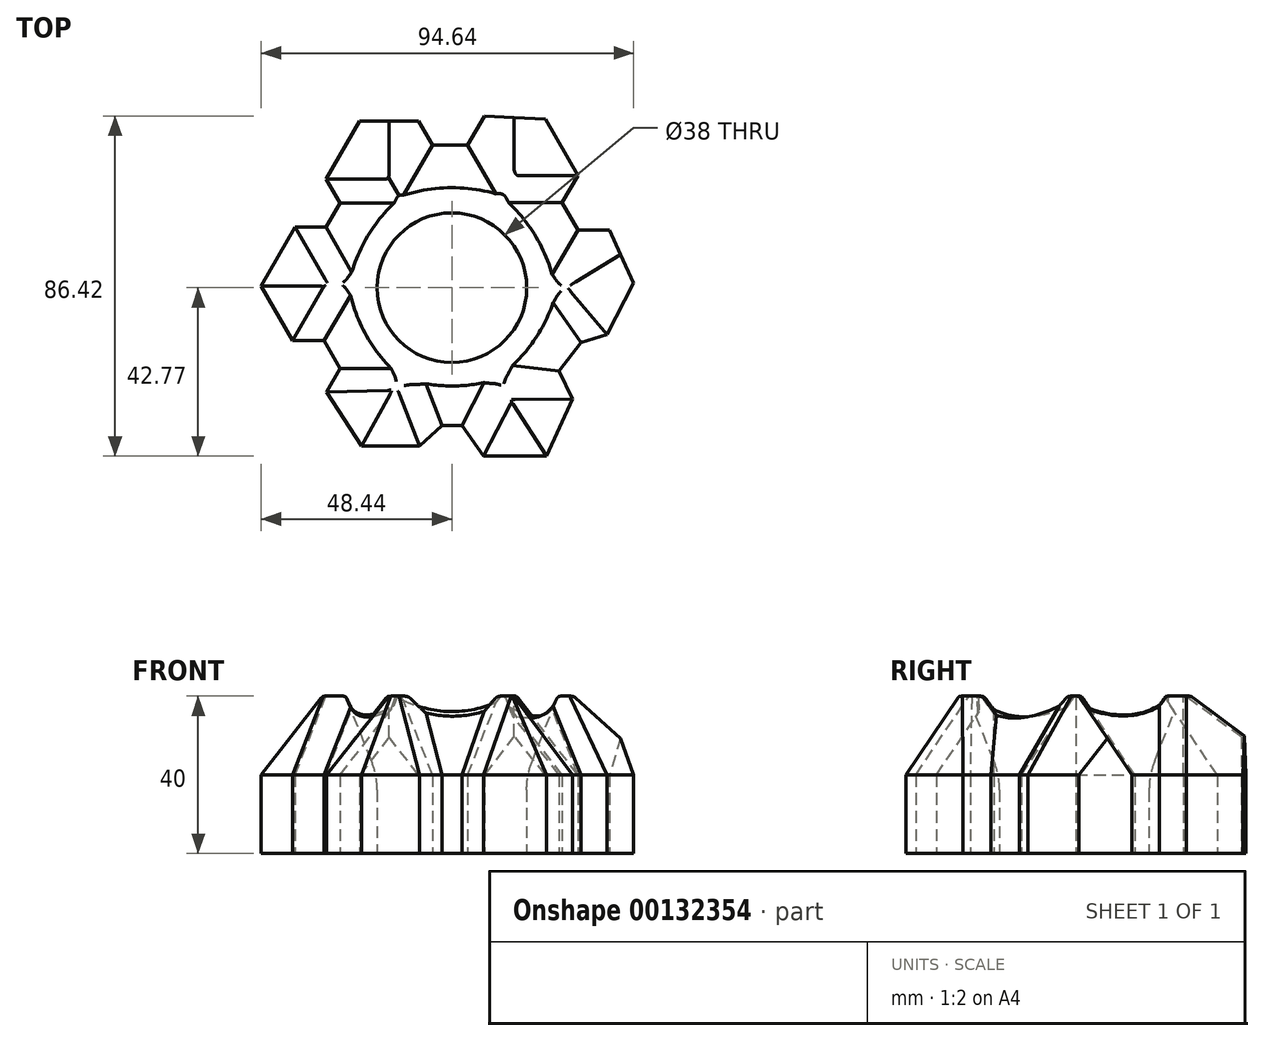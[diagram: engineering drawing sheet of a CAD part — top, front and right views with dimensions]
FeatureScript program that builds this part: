
annotation { "Feature Type Name" : "Feature", "Feature Type Description" : "" }
export const myFeature = defineFeature(function(context is Context, id is Id, definition is map)
    precondition{}
    {
        {
            var Q0;
            Q0=qCreatedBy(makeId("Top.planeOp"),FACE);
            var sketch = newSketch(context, id + "F0", { "sketchPlane" : qUnion([Q0])});
            skLineSegment(sketch, "E0", {"start": v(-48.44, 0.38) * mm, "end": v(-39.8, 15.35) * mm});
            skLineSegment(sketch, "E1", {"start": v(-39.8, 15.35) * mm, "end": v(-31.98, 15.35) * mm});
            skLineSegment(sketch, "E2", {"start": v(-31.98, 15.35) * mm, "end": v(-28.4, 21.56) * mm});
            skLineSegment(sketch, "E3", {"start": v(-28.4, 21.56) * mm, "end": v(-31.92, 27.66) * mm});
            skLineSegment(sketch, "E4", {"start": v(-31.92, 27.66) * mm, "end": v(-23.42, 42.38) * mm});
            skLineSegment(sketch, "E5", {"start": v(-23.42, 42.38) * mm, "end": v(-8.47, 42.38) * mm});
            skLineSegment(sketch, "E6", {"start": v(-8.47, 42.38) * mm, "end": v(-4.96, 36.29) * mm});
            skLineSegment(sketch, "E7", {"start": v(-4.96, 36.29) * mm, "end": v(4.04, 36.29) * mm});
            skLineSegment(sketch, "E8", {"start": v(4.04, 36.29) * mm, "end": v(8.3, 43.65) * mm});
            skLineSegment(sketch, "E9", {"start": v(8.3, 43.65) * mm, "end": v(23.77, 42.82) * mm});
            skLineSegment(sketch, "E10", {"start": v(23.77, 42.82) * mm, "end": v(32.02, 28.53) * mm});
            skLineSegment(sketch, "E11", {"start": v(32.02, 28.53) * mm, "end": v(28.02, 21.6) * mm});
            skLineSegment(sketch, "E12", {"start": v(28.02, 21.6) * mm, "end": v(32.02, 14.67) * mm});
            skLineSegment(sketch, "E13", {"start": v(32.02, 14.67) * mm, "end": v(40.02, 14.67) * mm});
            skLineSegment(sketch, "E14", {"start": v(-48.44, 0.38) * mm, "end": v(-40.44, -13.47) * mm});
            skLineSegment(sketch, "E15", {"start": v(-40.44, -13.47) * mm, "end": v(-32.44, -13.47) * mm});
            skLineSegment(sketch, "E16", {"start": v(-32.44, -13.47) * mm, "end": v(-28.4, -20.47) * mm});
            skLineSegment(sketch, "E17", {"start": v(-28.4, -20.47) * mm, "end": v(-31.85, -26.44) * mm});
            skLineSegment(sketch, "E18", {"start": v(24.09, -42.77) * mm, "end": v(8.09, -42.77) * mm});
            skLineSegment(sketch, "E19", {"start": v(8.09, -42.77) * mm, "end": v(2.53, -35.02) * mm});
            skCircle(sketch, "E20", {"center": v(0, 0) * mm, "radius": 19 * mm});
            skLineSegment(sketch, "E21", {"start": v(2.53, -35.02) * mm, "end": v(-2.47, -35.02) * mm});
            skLineSegment(sketch, "E22", {"start": v(-2.47, -35.02) * mm, "end": v(-8.17, -40.27) * mm});
            skLineSegment(sketch, "E23", {"start": v(-8.17, -40.27) * mm, "end": v(-22.93, -40.27) * mm});
            skLineSegment(sketch, "E24", {"start": v(-22.93, -40.27) * mm, "end": v(-31.85, -26.44) * mm});
            skLineSegment(sketch, "E25", {"start": v(40.02, 14.67) * mm, "end": v(46.2, 1.16) * mm});
            skLineSegment(sketch, "E26", {"start": v(46.2, 1.16) * mm, "end": v(39.38, -11.85) * mm});
            skLineSegment(sketch, "E27", {"start": v(39.38, -11.85) * mm, "end": v(32.82, -13.96) * mm});
            skLineSegment(sketch, "E28", {"start": v(32.82, -13.96) * mm, "end": v(27.24, -21.14) * mm});
            skLineSegment(sketch, "E29", {"start": v(27.24, -21.14) * mm, "end": v(30.59, -28.33) * mm});
            skLineSegment(sketch, "E30", {"start": v(30.59, -28.33) * mm, "end": v(24.09, -42.77) * mm});
            skSolve(sketch);
        }
        {
            var Q0;
            Q0 = qSketchRegion(id + "F0", true);
            extrude(context, id + "F1", {"entities" : qUnion([Q0]), "depth" : 40 * mm});
        }
        {
            var Q0;
            Q0=makeQuery(id+"F1.opExtrude","CAP_EDGE",EDGE,{"disambiguationData":[OSD([sQuery(id+"F0.wireOp",EDGE,"QNCMXTpP-GXVm-6eRc-1OdR-BgQgE8rH5RGP")])],"isStart":false});
            var Q1;
            Q1=makeQuery(id+"F1.opExtrude","CAP_EDGE",EDGE,{"disambiguationData":[OSD([sQuery(id+"F0.wireOp",EDGE,"32e85595-2d38-4c8c-88ba-0e2045ae9be3.filletArc")])],"isStart":false});
            var Q2;
            Q2=makeQuery(id+"F1.opExtrude","CAP_EDGE",EDGE,{"disambiguationData":[OSD([sQuery(id+"F0.wireOp",EDGE,"7Lfb2Pw1-ovII-kQZP-8tTO-OoWHJU2uK7MA")])],"isStart":false});
            var Q3;
            Q3=makeQuery(id+"F1.opExtrude","CAP_EDGE",EDGE,{"disambiguationData":[OSD([sQuery(id+"F0.wireOp",EDGE,"GPxmBkKN-ensr-DpaE-CKd3-DWqYEm3aYaC1")])],"isStart":false});
            var Q4;
            Q4=makeQuery(id+"F1.opExtrude","CAP_EDGE",EDGE,{"disambiguationData":[OSD([sQuery(id+"F0.wireOp",EDGE,"cDQV9YWy-g1bv-AJuI-bAqr-Qak8u58BYPGV")])],"isStart":false});
            var Q5;
            Q5=makeQuery(id+"F1.opExtrude","CAP_EDGE",EDGE,{"disambiguationData":[OSD([sQuery(id+"F0.wireOp",EDGE,"83e46631-e496-48b3-ba96-4f3d211e591d.filletArc")])],"isStart":false});
            var Q6;
            Q6=makeQuery(id+"F1.opExtrude","CAP_EDGE",EDGE,{"disambiguationData":[OSD([sQuery(id+"F0.wireOp",EDGE,"998c5da3-717e-4341-962a-c66db3e48c3c.filletArc")])],"isStart":false});
            var Q7;
            Q7=makeQuery(id+"F1.opExtrude","CAP_EDGE",EDGE,{"disambiguationData":[OSD([sQuery(id+"F0.wireOp",EDGE,"pI0UNvur-lg5A-7E1c-7WQA-sV9YhzP1md2U")])],"isStart":false});
            var Q8;
            Q8=makeQuery(id+"F1.opExtrude","CAP_EDGE",EDGE,{"disambiguationData":[OSD([sQuery(id+"F0.wireOp",EDGE,"E13")])],"isStart":false});
            var Q9;
            Q9=makeQuery(id+"F1.opExtrude","CAP_EDGE",EDGE,{"disambiguationData":[OSD([sQuery(id+"F0.wireOp",EDGE,"E12")])],"isStart":false});
            var Q10;
            Q10=makeQuery(id+"F1.opExtrude","CAP_EDGE",EDGE,{"disambiguationData":[OSD([sQuery(id+"F0.wireOp",EDGE,"E11")])],"isStart":false});
            var Q11;
            Q11=makeQuery(id+"F1.opExtrude","CAP_EDGE",EDGE,{"disambiguationData":[OSD([sQuery(id+"F0.wireOp",EDGE,"E10")])],"isStart":false});
            var Q12;
            Q12=makeQuery(id+"F1.opExtrude","CAP_EDGE",EDGE,{"disambiguationData":[OSD([sQuery(id+"F0.wireOp",EDGE,"E9")])],"isStart":false});
            var Q13;
            Q13=makeQuery(id+"F1.opExtrude","CAP_EDGE",EDGE,{"disambiguationData":[OSD([sQuery(id+"F0.wireOp",EDGE,"E8")])],"isStart":false});
            var Q14;
            Q14=makeQuery(id+"F1.opExtrude","CAP_EDGE",EDGE,{"disambiguationData":[OSD([sQuery(id+"F0.wireOp",EDGE,"E7")])],"isStart":false});
            var Q15;
            Q15=makeQuery(id+"F1.opExtrude","CAP_EDGE",EDGE,{"disambiguationData":[OSD([sQuery(id+"F0.wireOp",EDGE,"E6")])],"isStart":false});
            var Q16;
            Q16=makeQuery(id+"F1.opExtrude","CAP_EDGE",EDGE,{"disambiguationData":[OSD([sQuery(id+"F0.wireOp",EDGE,"E5")])],"isStart":false});
            var Q17;
            Q17=makeQuery(id+"F1.opExtrude","CAP_EDGE",EDGE,{"disambiguationData":[OSD([sQuery(id+"F0.wireOp",EDGE,"E4")])],"isStart":false});
            var Q18;
            Q18=makeQuery(id+"F1.opExtrude","CAP_EDGE",EDGE,{"disambiguationData":[OSD([sQuery(id+"F0.wireOp",EDGE,"E3")])],"isStart":false});
            var Q19;
            Q19=makeQuery(id+"F1.opExtrude","CAP_EDGE",EDGE,{"disambiguationData":[OSD([sQuery(id+"F0.wireOp",EDGE,"E2")])],"isStart":false});
            var Q20;
            Q20=makeQuery(id+"F1.opExtrude","CAP_EDGE",EDGE,{"disambiguationData":[OSD([sQuery(id+"F0.wireOp",EDGE,"E1")])],"isStart":false});
            var Q21;
            Q21=makeQuery(id+"F1.opExtrude","CAP_EDGE",EDGE,{"disambiguationData":[OSD([sQuery(id+"F0.wireOp",EDGE,"E0")])],"isStart":false});
            var Q22;
            Q22=makeQuery(id+"F1.opExtrude","CAP_EDGE",EDGE,{"disambiguationData":[OSD([sQuery(id+"F0.wireOp",EDGE,"E14")])],"isStart":false});
            var Q23;
            Q23=makeQuery(id+"F1.opExtrude","CAP_EDGE",EDGE,{"disambiguationData":[OSD([sQuery(id+"F0.wireOp",EDGE,"E15")])],"isStart":false});
            var Q24;
            Q24=makeQuery(id+"F1.opExtrude","CAP_EDGE",EDGE,{"disambiguationData":[OSD([sQuery(id+"F0.wireOp",EDGE,"E16")])],"isStart":false});
            var Q25;
            Q25=makeQuery(id+"F1.opExtrude","CAP_EDGE",EDGE,{"disambiguationData":[OSD([sQuery(id+"F0.wireOp",EDGE,"E17")])],"isStart":false});
            var Q26;
            Q26=makeQuery(id+"F1.opExtrude","CAP_EDGE",EDGE,{"disambiguationData":[OSD([sQuery(id+"F0.wireOp",EDGE,"E24")])],"isStart":false});
            var Q27;
            Q27=makeQuery(id+"F1.opExtrude","CAP_EDGE",EDGE,{"disambiguationData":[OSD([sQuery(id+"F0.wireOp",EDGE,"E23")])],"isStart":false});
            var Q28;
            Q28=makeQuery(id+"F1.opExtrude","CAP_EDGE",EDGE,{"disambiguationData":[OSD([sQuery(id+"F0.wireOp",EDGE,"E22")])],"isStart":false});
            var Q29;
            Q29=makeQuery(id+"F1.opExtrude","CAP_EDGE",EDGE,{"disambiguationData":[OSD([sQuery(id+"F0.wireOp",EDGE,"E21")])],"isStart":false});
            var Q30;
            Q30=makeQuery(id+"F1.opExtrude","CAP_EDGE",EDGE,{"disambiguationData":[OSD([sQuery(id+"F0.wireOp",EDGE,"E19")])],"isStart":false});
            var Q31;
            Q31=makeQuery(id+"F1.opExtrude","CAP_EDGE",EDGE,{"disambiguationData":[OSD([sQuery(id+"F0.wireOp",EDGE,"E18")])],"isStart":false});
            var Q32;
            Q32=makeQuery(id+"F1.opExtrude","CAP_EDGE",EDGE,{"disambiguationData":[OSD([sQuery(id+"F0.wireOp",EDGE,"E30")])],"isStart":false});
            var Q33;
            Q33=makeQuery(id+"F1.opExtrude","CAP_EDGE",EDGE,{"disambiguationData":[OSD([sQuery(id+"F0.wireOp",EDGE,"E29")])],"isStart":false});
            var Q34;
            Q34=makeQuery(id+"F1.opExtrude","CAP_EDGE",EDGE,{"disambiguationData":[OSD([sQuery(id+"F0.wireOp",EDGE,"E28")])],"isStart":false});
            var Q35;
            Q35=makeQuery(id+"F1.opExtrude","CAP_EDGE",EDGE,{"disambiguationData":[OSD([sQuery(id+"F0.wireOp",EDGE,"E27")])],"isStart":false});
            var Q36;
            Q36=makeQuery(id+"F1.opExtrude","CAP_EDGE",EDGE,{"disambiguationData":[OSD([sQuery(id+"F0.wireOp",EDGE,"E26")])],"isStart":false});
            var Q37;
            Q37=makeQuery(id+"F1.opExtrude","CAP_EDGE",EDGE,{"disambiguationData":[OSD([sQuery(id+"F0.wireOp",EDGE,"E25")])],"isStart":false});
            chamfer(context, id + "F2", {"entities" : qUnion([Q0, Q1, Q2, Q3, Q4, Q5, Q6, Q7, Q8, Q9, Q10, Q11, Q12, Q13, Q14, Q15, Q16, Q17, Q18, Q19, Q20, Q21, Q22, Q23, Q24, Q25, Q26, Q27, Q28, Q29, Q30, Q31, Q32, Q33, Q34, Q35, Q36, Q37]), "chamferType" : ChamferType.TWO_OFFSETS, "width1" : 20 * mm, "oppositeDirection" : false, "width2" : 13.5 * mm, "tangentPropagation" : true});
        }
        {
            var Q0;
            Q0=makeQuery(id+"F1.opExtrude","CAP_EDGE",EDGE,{"disambiguationData":[OSD([sQuery(id+"F0.wireOp",EDGE,"E20")])],"isStart":false});
            chamfer(context, id + "F3", {"entities" : qUnion([Q0]), "chamferType" : ChamferType.TWO_OFFSETS, "width1" : 20 * mm, "oppositeDirection" : false, "width2" : 8 * mm, "tangentPropagation" : true});
        }
        {
            var Q0;
            Q0=makeQuery(id+"F3.opChamfer","SPLIT",FACE,{"disambiguationData":[OD(0.0)],"derivedFrom":makeQuery(id+"F1.opExtrude","CAP_FACE",FACE,{"disambiguationData":[OSD([sQuery(id+"F0.wireOp",EDGE,"E0"),sQuery(id+"F0.wireOp",EDGE,"E1"),sQuery(id+"F0.wireOp",EDGE,"E2"),sQuery(id+"F0.wireOp",EDGE,"E3"),sQuery(id+"F0.wireOp",EDGE,"E4"),sQuery(id+"F0.wireOp",EDGE,"E5"),sQuery(id+"F0.wireOp",EDGE,"E6"),sQuery(id+"F0.wireOp",EDGE,"E7"),sQuery(id+"F0.wireOp",EDGE,"E8"),sQuery(id+"F0.wireOp",EDGE,"E9"),sQuery(id+"F0.wireOp",EDGE,"E10"),sQuery(id+"F0.wireOp",EDGE,"E11"),sQuery(id+"F0.wireOp",EDGE,"E12"),sQuery(id+"F0.wireOp",EDGE,"E13"),sQuery(id+"F0.wireOp",EDGE,"E14"),sQuery(id+"F0.wireOp",EDGE,"E15"),sQuery(id+"F0.wireOp",EDGE,"E16"),sQuery(id+"F0.wireOp",EDGE,"E17"),sQuery(id+"F0.wireOp",EDGE,"E18"),sQuery(id+"F0.wireOp",EDGE,"E19"),sQuery(id+"F0.wireOp",EDGE,"E20"),sQuery(id+"F0.wireOp",EDGE,"E21"),sQuery(id+"F0.wireOp",EDGE,"E22"),sQuery(id+"F0.wireOp",EDGE,"E23"),sQuery(id+"F0.wireOp",EDGE,"E24"),sQuery(id+"F0.wireOp",EDGE,"E25"),sQuery(id+"F0.wireOp",EDGE,"E26"),sQuery(id+"F0.wireOp",EDGE,"E27"),sQuery(id+"F0.wireOp",EDGE,"E28"),sQuery(id+"F0.wireOp",EDGE,"E29"),sQuery(id+"F0.wireOp",EDGE,"E30")])],"isStart":false})});
            var Q1;
            {var subQ0=sQuery(id+"F0.wireOp",EDGE,"E6");Q1=makeQuery(id+"F2.opChamfer","BLEND_EDGE",EDGE,{"blendedFrom":[makeQuery(id+"F1.opExtrude","CAP_EDGE",EDGE,{"disambiguationData":[OSD([subQ0])],"isStart":false}),makeQuery(id+"F1.opExtrude","CAP_FACE",FACE,{"disambiguationData":[OSD([sQuery(id+"F0.wireOp",EDGE,"E0"),sQuery(id+"F0.wireOp",EDGE,"E1"),sQuery(id+"F0.wireOp",EDGE,"E2"),sQuery(id+"F0.wireOp",EDGE,"E3"),sQuery(id+"F0.wireOp",EDGE,"E4"),sQuery(id+"F0.wireOp",EDGE,"E5"),subQ0,sQuery(id+"F0.wireOp",EDGE,"E7"),sQuery(id+"F0.wireOp",EDGE,"E8"),sQuery(id+"F0.wireOp",EDGE,"E9"),sQuery(id+"F0.wireOp",EDGE,"E10"),sQuery(id+"F0.wireOp",EDGE,"E11"),sQuery(id+"F0.wireOp",EDGE,"E12"),sQuery(id+"F0.wireOp",EDGE,"E13"),sQuery(id+"F0.wireOp",EDGE,"E14"),sQuery(id+"F0.wireOp",EDGE,"E15"),sQuery(id+"F0.wireOp",EDGE,"E16"),sQuery(id+"F0.wireOp",EDGE,"E17"),sQuery(id+"F0.wireOp",EDGE,"E18"),sQuery(id+"F0.wireOp",EDGE,"E19"),sQuery(id+"F0.wireOp",EDGE,"E20"),sQuery(id+"F0.wireOp",EDGE,"E21"),sQuery(id+"F0.wireOp",EDGE,"E22"),sQuery(id+"F0.wireOp",EDGE,"E23"),sQuery(id+"F0.wireOp",EDGE,"E24"),sQuery(id+"F0.wireOp",EDGE,"E25"),sQuery(id+"F0.wireOp",EDGE,"E26"),sQuery(id+"F0.wireOp",EDGE,"E27"),sQuery(id+"F0.wireOp",EDGE,"E28"),sQuery(id+"F0.wireOp",EDGE,"E29"),sQuery(id+"F0.wireOp",EDGE,"E30")])],"isStart":false})],"blendedInto":[makeQuery(id+"F1.opExtrude","CAP_FACE",FACE,{"disambiguationData":[OSD([sQuery(id+"F0.wireOp",EDGE,"E0"),sQuery(id+"F0.wireOp",EDGE,"E1"),sQuery(id+"F0.wireOp",EDGE,"E2"),sQuery(id+"F0.wireOp",EDGE,"E3"),sQuery(id+"F0.wireOp",EDGE,"E4"),sQuery(id+"F0.wireOp",EDGE,"E5"),subQ0,sQuery(id+"F0.wireOp",EDGE,"E7"),sQuery(id+"F0.wireOp",EDGE,"E8"),sQuery(id+"F0.wireOp",EDGE,"E9"),sQuery(id+"F0.wireOp",EDGE,"E10"),sQuery(id+"F0.wireOp",EDGE,"E11"),sQuery(id+"F0.wireOp",EDGE,"E12"),sQuery(id+"F0.wireOp",EDGE,"E13"),sQuery(id+"F0.wireOp",EDGE,"E14"),sQuery(id+"F0.wireOp",EDGE,"E15"),sQuery(id+"F0.wireOp",EDGE,"E16"),sQuery(id+"F0.wireOp",EDGE,"E17"),sQuery(id+"F0.wireOp",EDGE,"E18"),sQuery(id+"F0.wireOp",EDGE,"E19"),sQuery(id+"F0.wireOp",EDGE,"E20"),sQuery(id+"F0.wireOp",EDGE,"E21"),sQuery(id+"F0.wireOp",EDGE,"E22"),sQuery(id+"F0.wireOp",EDGE,"E23"),sQuery(id+"F0.wireOp",EDGE,"E24"),sQuery(id+"F0.wireOp",EDGE,"E25"),sQuery(id+"F0.wireOp",EDGE,"E26"),sQuery(id+"F0.wireOp",EDGE,"E27"),sQuery(id+"F0.wireOp",EDGE,"E28"),sQuery(id+"F0.wireOp",EDGE,"E29"),sQuery(id+"F0.wireOp",EDGE,"E30")])],"isStart":false})]});}
            var Q2;
            {var subQ0=sQuery(id+"F0.wireOp",EDGE,"E3");Q2=makeQuery(id+"F2.opChamfer","BLEND_EDGE",EDGE,{"blendedFrom":[makeQuery(id+"F1.opExtrude","CAP_EDGE",EDGE,{"disambiguationData":[OSD([subQ0])],"isStart":false}),makeQuery(id+"F1.opExtrude","CAP_FACE",FACE,{"disambiguationData":[OSD([sQuery(id+"F0.wireOp",EDGE,"E0"),sQuery(id+"F0.wireOp",EDGE,"E1"),sQuery(id+"F0.wireOp",EDGE,"E2"),subQ0,sQuery(id+"F0.wireOp",EDGE,"E4"),sQuery(id+"F0.wireOp",EDGE,"E5"),sQuery(id+"F0.wireOp",EDGE,"E6"),sQuery(id+"F0.wireOp",EDGE,"E7"),sQuery(id+"F0.wireOp",EDGE,"E8"),sQuery(id+"F0.wireOp",EDGE,"E9"),sQuery(id+"F0.wireOp",EDGE,"E10"),sQuery(id+"F0.wireOp",EDGE,"E11"),sQuery(id+"F0.wireOp",EDGE,"E12"),sQuery(id+"F0.wireOp",EDGE,"E13"),sQuery(id+"F0.wireOp",EDGE,"E14"),sQuery(id+"F0.wireOp",EDGE,"E15"),sQuery(id+"F0.wireOp",EDGE,"E16"),sQuery(id+"F0.wireOp",EDGE,"E17"),sQuery(id+"F0.wireOp",EDGE,"E18"),sQuery(id+"F0.wireOp",EDGE,"E19"),sQuery(id+"F0.wireOp",EDGE,"E20"),sQuery(id+"F0.wireOp",EDGE,"E21"),sQuery(id+"F0.wireOp",EDGE,"E22"),sQuery(id+"F0.wireOp",EDGE,"E23"),sQuery(id+"F0.wireOp",EDGE,"E24"),sQuery(id+"F0.wireOp",EDGE,"E25"),sQuery(id+"F0.wireOp",EDGE,"E26"),sQuery(id+"F0.wireOp",EDGE,"E27"),sQuery(id+"F0.wireOp",EDGE,"E28"),sQuery(id+"F0.wireOp",EDGE,"E29"),sQuery(id+"F0.wireOp",EDGE,"E30")])],"isStart":false})],"blendedInto":[makeQuery(id+"F1.opExtrude","CAP_FACE",FACE,{"disambiguationData":[OSD([sQuery(id+"F0.wireOp",EDGE,"E0"),sQuery(id+"F0.wireOp",EDGE,"E1"),sQuery(id+"F0.wireOp",EDGE,"E2"),subQ0,sQuery(id+"F0.wireOp",EDGE,"E4"),sQuery(id+"F0.wireOp",EDGE,"E5"),sQuery(id+"F0.wireOp",EDGE,"E6"),sQuery(id+"F0.wireOp",EDGE,"E7"),sQuery(id+"F0.wireOp",EDGE,"E8"),sQuery(id+"F0.wireOp",EDGE,"E9"),sQuery(id+"F0.wireOp",EDGE,"E10"),sQuery(id+"F0.wireOp",EDGE,"E11"),sQuery(id+"F0.wireOp",EDGE,"E12"),sQuery(id+"F0.wireOp",EDGE,"E13"),sQuery(id+"F0.wireOp",EDGE,"E14"),sQuery(id+"F0.wireOp",EDGE,"E15"),sQuery(id+"F0.wireOp",EDGE,"E16"),sQuery(id+"F0.wireOp",EDGE,"E17"),sQuery(id+"F0.wireOp",EDGE,"E18"),sQuery(id+"F0.wireOp",EDGE,"E19"),sQuery(id+"F0.wireOp",EDGE,"E20"),sQuery(id+"F0.wireOp",EDGE,"E21"),sQuery(id+"F0.wireOp",EDGE,"E22"),sQuery(id+"F0.wireOp",EDGE,"E23"),sQuery(id+"F0.wireOp",EDGE,"E24"),sQuery(id+"F0.wireOp",EDGE,"E25"),sQuery(id+"F0.wireOp",EDGE,"E26"),sQuery(id+"F0.wireOp",EDGE,"E27"),sQuery(id+"F0.wireOp",EDGE,"E28"),sQuery(id+"F0.wireOp",EDGE,"E29"),sQuery(id+"F0.wireOp",EDGE,"E30")])],"isStart":false})]});}
            var Q3;
            {var subQ0=sQuery(id+"F0.wireOp",EDGE,"E11");Q3=makeQuery(id+"F2.opChamfer","BLEND_EDGE",EDGE,{"blendedFrom":[makeQuery(id+"F1.opExtrude","CAP_EDGE",EDGE,{"disambiguationData":[OSD([subQ0])],"isStart":false}),makeQuery(id+"F1.opExtrude","CAP_FACE",FACE,{"disambiguationData":[OSD([sQuery(id+"F0.wireOp",EDGE,"E0"),sQuery(id+"F0.wireOp",EDGE,"E1"),sQuery(id+"F0.wireOp",EDGE,"E2"),sQuery(id+"F0.wireOp",EDGE,"E3"),sQuery(id+"F0.wireOp",EDGE,"E4"),sQuery(id+"F0.wireOp",EDGE,"E5"),sQuery(id+"F0.wireOp",EDGE,"E6"),sQuery(id+"F0.wireOp",EDGE,"E7"),sQuery(id+"F0.wireOp",EDGE,"E8"),sQuery(id+"F0.wireOp",EDGE,"E9"),sQuery(id+"F0.wireOp",EDGE,"E10"),subQ0,sQuery(id+"F0.wireOp",EDGE,"E12"),sQuery(id+"F0.wireOp",EDGE,"E13"),sQuery(id+"F0.wireOp",EDGE,"E14"),sQuery(id+"F0.wireOp",EDGE,"E15"),sQuery(id+"F0.wireOp",EDGE,"E16"),sQuery(id+"F0.wireOp",EDGE,"E17"),sQuery(id+"F0.wireOp",EDGE,"E18"),sQuery(id+"F0.wireOp",EDGE,"E19"),sQuery(id+"F0.wireOp",EDGE,"E20"),sQuery(id+"F0.wireOp",EDGE,"E21"),sQuery(id+"F0.wireOp",EDGE,"E22"),sQuery(id+"F0.wireOp",EDGE,"E23"),sQuery(id+"F0.wireOp",EDGE,"E24"),sQuery(id+"F0.wireOp",EDGE,"E25"),sQuery(id+"F0.wireOp",EDGE,"E26"),sQuery(id+"F0.wireOp",EDGE,"E27"),sQuery(id+"F0.wireOp",EDGE,"E28"),sQuery(id+"F0.wireOp",EDGE,"E29"),sQuery(id+"F0.wireOp",EDGE,"E30")])],"isStart":false})],"blendedInto":[makeQuery(id+"F1.opExtrude","CAP_FACE",FACE,{"disambiguationData":[OSD([sQuery(id+"F0.wireOp",EDGE,"E0"),sQuery(id+"F0.wireOp",EDGE,"E1"),sQuery(id+"F0.wireOp",EDGE,"E2"),sQuery(id+"F0.wireOp",EDGE,"E3"),sQuery(id+"F0.wireOp",EDGE,"E4"),sQuery(id+"F0.wireOp",EDGE,"E5"),sQuery(id+"F0.wireOp",EDGE,"E6"),sQuery(id+"F0.wireOp",EDGE,"E7"),sQuery(id+"F0.wireOp",EDGE,"E8"),sQuery(id+"F0.wireOp",EDGE,"E9"),sQuery(id+"F0.wireOp",EDGE,"E10"),subQ0,sQuery(id+"F0.wireOp",EDGE,"E12"),sQuery(id+"F0.wireOp",EDGE,"E13"),sQuery(id+"F0.wireOp",EDGE,"E14"),sQuery(id+"F0.wireOp",EDGE,"E15"),sQuery(id+"F0.wireOp",EDGE,"E16"),sQuery(id+"F0.wireOp",EDGE,"E17"),sQuery(id+"F0.wireOp",EDGE,"E18"),sQuery(id+"F0.wireOp",EDGE,"E19"),sQuery(id+"F0.wireOp",EDGE,"E20"),sQuery(id+"F0.wireOp",EDGE,"E21"),sQuery(id+"F0.wireOp",EDGE,"E22"),sQuery(id+"F0.wireOp",EDGE,"E23"),sQuery(id+"F0.wireOp",EDGE,"E24"),sQuery(id+"F0.wireOp",EDGE,"E25"),sQuery(id+"F0.wireOp",EDGE,"E26"),sQuery(id+"F0.wireOp",EDGE,"E27"),sQuery(id+"F0.wireOp",EDGE,"E28"),sQuery(id+"F0.wireOp",EDGE,"E29"),sQuery(id+"F0.wireOp",EDGE,"E30")])],"isStart":false})]});}
            var Q4;
            {var subQ0=sQuery(id+"F0.wireOp",EDGE,"E8");Q4=makeQuery(id+"F2.opChamfer","BLEND_EDGE",EDGE,{"blendedFrom":[makeQuery(id+"F1.opExtrude","CAP_EDGE",EDGE,{"disambiguationData":[OSD([subQ0])],"isStart":false}),makeQuery(id+"F1.opExtrude","CAP_FACE",FACE,{"disambiguationData":[OSD([sQuery(id+"F0.wireOp",EDGE,"E0"),sQuery(id+"F0.wireOp",EDGE,"E1"),sQuery(id+"F0.wireOp",EDGE,"E2"),sQuery(id+"F0.wireOp",EDGE,"E3"),sQuery(id+"F0.wireOp",EDGE,"E4"),sQuery(id+"F0.wireOp",EDGE,"E5"),sQuery(id+"F0.wireOp",EDGE,"E6"),sQuery(id+"F0.wireOp",EDGE,"E7"),subQ0,sQuery(id+"F0.wireOp",EDGE,"E9"),sQuery(id+"F0.wireOp",EDGE,"E10"),sQuery(id+"F0.wireOp",EDGE,"E11"),sQuery(id+"F0.wireOp",EDGE,"E12"),sQuery(id+"F0.wireOp",EDGE,"E13"),sQuery(id+"F0.wireOp",EDGE,"E14"),sQuery(id+"F0.wireOp",EDGE,"E15"),sQuery(id+"F0.wireOp",EDGE,"E16"),sQuery(id+"F0.wireOp",EDGE,"E17"),sQuery(id+"F0.wireOp",EDGE,"E18"),sQuery(id+"F0.wireOp",EDGE,"E19"),sQuery(id+"F0.wireOp",EDGE,"E20"),sQuery(id+"F0.wireOp",EDGE,"E21"),sQuery(id+"F0.wireOp",EDGE,"E22"),sQuery(id+"F0.wireOp",EDGE,"E23"),sQuery(id+"F0.wireOp",EDGE,"E24"),sQuery(id+"F0.wireOp",EDGE,"E25"),sQuery(id+"F0.wireOp",EDGE,"E26"),sQuery(id+"F0.wireOp",EDGE,"E27"),sQuery(id+"F0.wireOp",EDGE,"E28"),sQuery(id+"F0.wireOp",EDGE,"E29"),sQuery(id+"F0.wireOp",EDGE,"E30")])],"isStart":false})],"blendedInto":[makeQuery(id+"F1.opExtrude","CAP_FACE",FACE,{"disambiguationData":[OSD([sQuery(id+"F0.wireOp",EDGE,"E0"),sQuery(id+"F0.wireOp",EDGE,"E1"),sQuery(id+"F0.wireOp",EDGE,"E2"),sQuery(id+"F0.wireOp",EDGE,"E3"),sQuery(id+"F0.wireOp",EDGE,"E4"),sQuery(id+"F0.wireOp",EDGE,"E5"),sQuery(id+"F0.wireOp",EDGE,"E6"),sQuery(id+"F0.wireOp",EDGE,"E7"),subQ0,sQuery(id+"F0.wireOp",EDGE,"E9"),sQuery(id+"F0.wireOp",EDGE,"E10"),sQuery(id+"F0.wireOp",EDGE,"E11"),sQuery(id+"F0.wireOp",EDGE,"E12"),sQuery(id+"F0.wireOp",EDGE,"E13"),sQuery(id+"F0.wireOp",EDGE,"E14"),sQuery(id+"F0.wireOp",EDGE,"E15"),sQuery(id+"F0.wireOp",EDGE,"E16"),sQuery(id+"F0.wireOp",EDGE,"E17"),sQuery(id+"F0.wireOp",EDGE,"E18"),sQuery(id+"F0.wireOp",EDGE,"E19"),sQuery(id+"F0.wireOp",EDGE,"E20"),sQuery(id+"F0.wireOp",EDGE,"E21"),sQuery(id+"F0.wireOp",EDGE,"E22"),sQuery(id+"F0.wireOp",EDGE,"E23"),sQuery(id+"F0.wireOp",EDGE,"E24"),sQuery(id+"F0.wireOp",EDGE,"E25"),sQuery(id+"F0.wireOp",EDGE,"E26"),sQuery(id+"F0.wireOp",EDGE,"E27"),sQuery(id+"F0.wireOp",EDGE,"E28"),sQuery(id+"F0.wireOp",EDGE,"E29"),sQuery(id+"F0.wireOp",EDGE,"E30")])],"isStart":false})]});}
            var Q5;
            Q5=makeQuery(id+"F3.opChamfer","SPLIT",FACE,{"disambiguationData":[OD(5.0)],"derivedFrom":makeQuery(id+"F1.opExtrude","CAP_FACE",FACE,{"disambiguationData":[OSD([sQuery(id+"F0.wireOp",EDGE,"E0"),sQuery(id+"F0.wireOp",EDGE,"E1"),sQuery(id+"F0.wireOp",EDGE,"E2"),sQuery(id+"F0.wireOp",EDGE,"E3"),sQuery(id+"F0.wireOp",EDGE,"E4"),sQuery(id+"F0.wireOp",EDGE,"E5"),sQuery(id+"F0.wireOp",EDGE,"E6"),sQuery(id+"F0.wireOp",EDGE,"E7"),sQuery(id+"F0.wireOp",EDGE,"E8"),sQuery(id+"F0.wireOp",EDGE,"E9"),sQuery(id+"F0.wireOp",EDGE,"E10"),sQuery(id+"F0.wireOp",EDGE,"E11"),sQuery(id+"F0.wireOp",EDGE,"E12"),sQuery(id+"F0.wireOp",EDGE,"E13"),sQuery(id+"F0.wireOp",EDGE,"E14"),sQuery(id+"F0.wireOp",EDGE,"E15"),sQuery(id+"F0.wireOp",EDGE,"E16"),sQuery(id+"F0.wireOp",EDGE,"E17"),sQuery(id+"F0.wireOp",EDGE,"E18"),sQuery(id+"F0.wireOp",EDGE,"E19"),sQuery(id+"F0.wireOp",EDGE,"E20"),sQuery(id+"F0.wireOp",EDGE,"E21"),sQuery(id+"F0.wireOp",EDGE,"E22"),sQuery(id+"F0.wireOp",EDGE,"E23"),sQuery(id+"F0.wireOp",EDGE,"E24"),sQuery(id+"F0.wireOp",EDGE,"E25"),sQuery(id+"F0.wireOp",EDGE,"E26"),sQuery(id+"F0.wireOp",EDGE,"E27"),sQuery(id+"F0.wireOp",EDGE,"E28"),sQuery(id+"F0.wireOp",EDGE,"E29"),sQuery(id+"F0.wireOp",EDGE,"E30")])],"isStart":false})});
            var Q6;
            Q6=makeQuery(id+"F3.opChamfer","SPLIT",FACE,{"disambiguationData":[OD(3.0)],"derivedFrom":makeQuery(id+"F1.opExtrude","CAP_FACE",FACE,{"disambiguationData":[OSD([sQuery(id+"F0.wireOp",EDGE,"E0"),sQuery(id+"F0.wireOp",EDGE,"E1"),sQuery(id+"F0.wireOp",EDGE,"E2"),sQuery(id+"F0.wireOp",EDGE,"E3"),sQuery(id+"F0.wireOp",EDGE,"E4"),sQuery(id+"F0.wireOp",EDGE,"E5"),sQuery(id+"F0.wireOp",EDGE,"E6"),sQuery(id+"F0.wireOp",EDGE,"E7"),sQuery(id+"F0.wireOp",EDGE,"E8"),sQuery(id+"F0.wireOp",EDGE,"E9"),sQuery(id+"F0.wireOp",EDGE,"E10"),sQuery(id+"F0.wireOp",EDGE,"E11"),sQuery(id+"F0.wireOp",EDGE,"E12"),sQuery(id+"F0.wireOp",EDGE,"E13"),sQuery(id+"F0.wireOp",EDGE,"E14"),sQuery(id+"F0.wireOp",EDGE,"E15"),sQuery(id+"F0.wireOp",EDGE,"E16"),sQuery(id+"F0.wireOp",EDGE,"E17"),sQuery(id+"F0.wireOp",EDGE,"E18"),sQuery(id+"F0.wireOp",EDGE,"E19"),sQuery(id+"F0.wireOp",EDGE,"E20"),sQuery(id+"F0.wireOp",EDGE,"E21"),sQuery(id+"F0.wireOp",EDGE,"E22"),sQuery(id+"F0.wireOp",EDGE,"E23"),sQuery(id+"F0.wireOp",EDGE,"E24"),sQuery(id+"F0.wireOp",EDGE,"E25"),sQuery(id+"F0.wireOp",EDGE,"E26"),sQuery(id+"F0.wireOp",EDGE,"E27"),sQuery(id+"F0.wireOp",EDGE,"E28"),sQuery(id+"F0.wireOp",EDGE,"E29"),sQuery(id+"F0.wireOp",EDGE,"E30")])],"isStart":false})});
            var Q7;
            Q7=makeQuery(id+"F3.opChamfer","SPLIT",FACE,{"disambiguationData":[OD(4.0)],"derivedFrom":makeQuery(id+"F1.opExtrude","CAP_FACE",FACE,{"disambiguationData":[OSD([sQuery(id+"F0.wireOp",EDGE,"E0"),sQuery(id+"F0.wireOp",EDGE,"E1"),sQuery(id+"F0.wireOp",EDGE,"E2"),sQuery(id+"F0.wireOp",EDGE,"E3"),sQuery(id+"F0.wireOp",EDGE,"E4"),sQuery(id+"F0.wireOp",EDGE,"E5"),sQuery(id+"F0.wireOp",EDGE,"E6"),sQuery(id+"F0.wireOp",EDGE,"E7"),sQuery(id+"F0.wireOp",EDGE,"E8"),sQuery(id+"F0.wireOp",EDGE,"E9"),sQuery(id+"F0.wireOp",EDGE,"E10"),sQuery(id+"F0.wireOp",EDGE,"E11"),sQuery(id+"F0.wireOp",EDGE,"E12"),sQuery(id+"F0.wireOp",EDGE,"E13"),sQuery(id+"F0.wireOp",EDGE,"E14"),sQuery(id+"F0.wireOp",EDGE,"E15"),sQuery(id+"F0.wireOp",EDGE,"E16"),sQuery(id+"F0.wireOp",EDGE,"E17"),sQuery(id+"F0.wireOp",EDGE,"E18"),sQuery(id+"F0.wireOp",EDGE,"E19"),sQuery(id+"F0.wireOp",EDGE,"E20"),sQuery(id+"F0.wireOp",EDGE,"E21"),sQuery(id+"F0.wireOp",EDGE,"E22"),sQuery(id+"F0.wireOp",EDGE,"E23"),sQuery(id+"F0.wireOp",EDGE,"E24"),sQuery(id+"F0.wireOp",EDGE,"E25"),sQuery(id+"F0.wireOp",EDGE,"E26"),sQuery(id+"F0.wireOp",EDGE,"E27"),sQuery(id+"F0.wireOp",EDGE,"E28"),sQuery(id+"F0.wireOp",EDGE,"E29"),sQuery(id+"F0.wireOp",EDGE,"E30")])],"isStart":false})});
            fillet(context, id + "F4", {"entities" : qUnion([Q0, Q1, Q2, Q3, Q4, Q5, Q6, Q7]), "radius" : 1 * mm, "tangentPropagation" : true, "allowEdgeOverflow" : false});
        }
        {
            var Q0;
            {var subQ0=sQuery(id+"F0.wireOp",EDGE,"E20");Q0=makeQuery(id+"F3.opChamfer","BLEND_EDGE",EDGE,{"blendedFrom":[makeQuery(id+"F1.opExtrude","CAP_EDGE",EDGE,{"disambiguationData":[OSD([subQ0])],"isStart":false}),makeQuery(id+"F1.opExtrude","SWEPT_FACE",FACE,{"disambiguationData":[OSD([subQ0])]})],"blendedInto":[makeQuery(id+"F1.opExtrude","SWEPT_FACE",FACE,{"disambiguationData":[OSD([subQ0])]})]});}
            fillet(context, id + "F5", {"entities" : qUnion([Q0]), "radius" : 20 * mm, "tangentPropagation" : true, "allowEdgeOverflow" : false});
        }
    });
